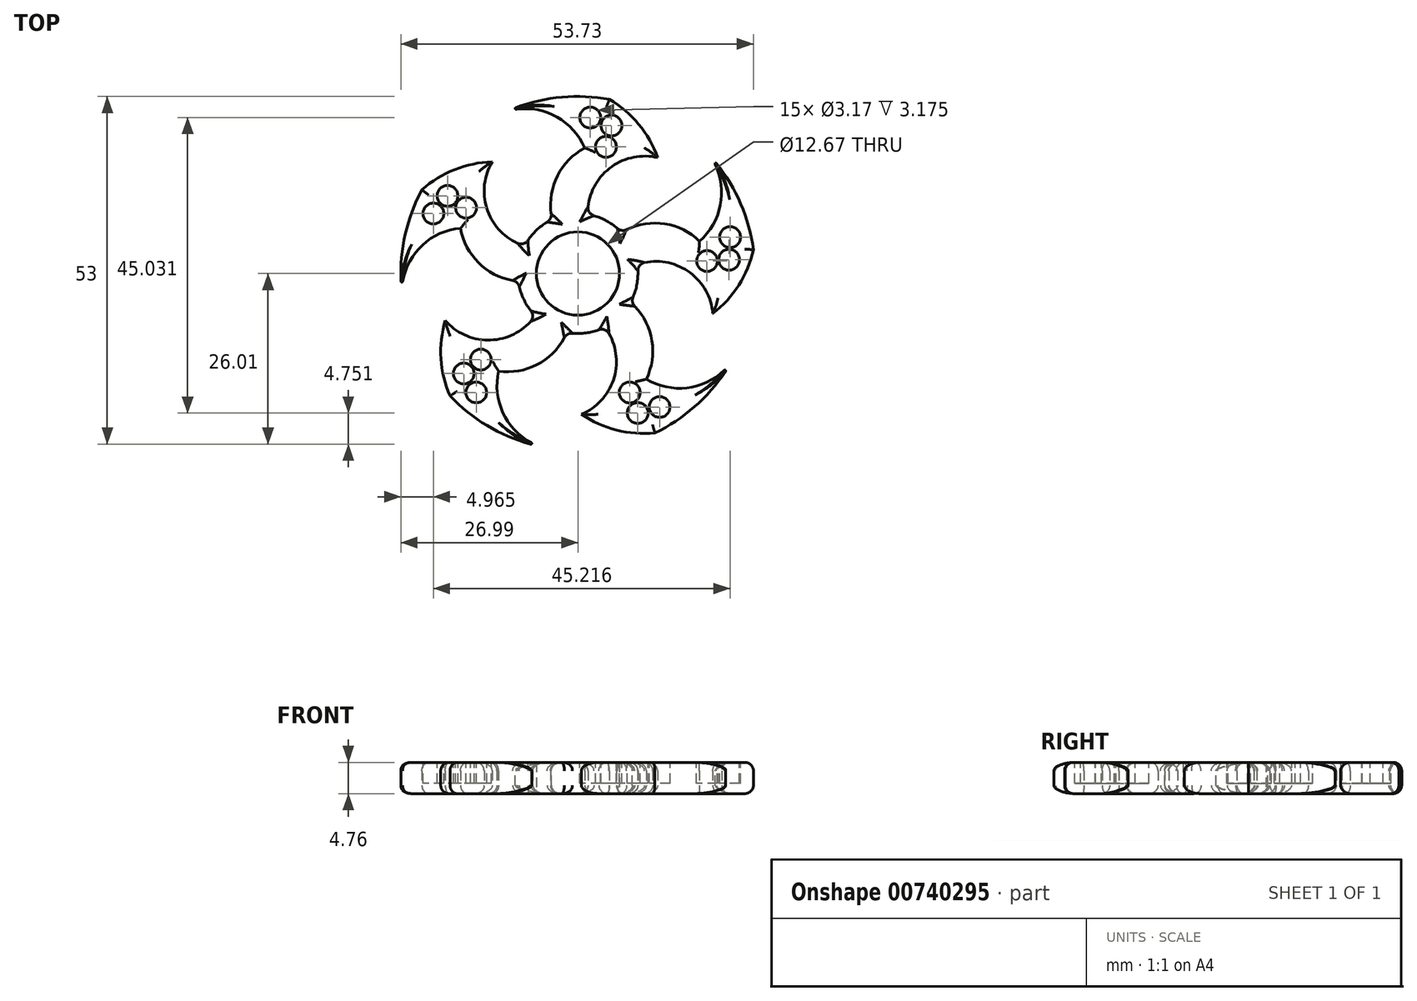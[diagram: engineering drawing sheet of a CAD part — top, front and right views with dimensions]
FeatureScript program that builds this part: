
annotation { "Feature Type Name" : "Feature", "Feature Type Description" : "" }
export const myFeature = defineFeature(function(context is Context, id is Id, definition is map)
    precondition{}
    {
        {
            var Q0;
            Q0=qCreatedBy(makeId("Top.planeOp"),FACE);
            var sketch = newSketch(context, id + "F0", { "sketchPlane" : qUnion([Q0])});
            skCircle(sketch, "E0", {"center": v(0, 0) * mm, "radius": 6.34 * mm});
            skArc(sketch, "E1", {"start": v(-9.07, -1.17) * mm, "mid": v(-8.22, -4) * mm, "end": v(-6.5, -6.43) * mm});
            skArc(sketch, "E2", {"start": v(-23.78, 12.77) * mm, "mid": v(-26.47, 5.28) * mm, "end": v(-26.86, -2.67) * mm});
            skArc(sketch, "E3", {"start": v(-17.89, 6.9) * mm, "mid": v(-24.2, 3.83) * mm, "end": v(-26.86, -2.67) * mm});
            skArc(sketch, "E4", {"start": v(-13.04, 17.02) * mm, "mid": v(-18.79, 15.84) * mm, "end": v(-23.78, 12.77) * mm});
            skArc(sketch, "E5", {"start": v(-17.89, 6.9) * mm, "mid": v(-14.85, 1.36) * mm, "end": v(-9.07, -1.17) * mm});
            skArc(sketch, "E6", {"start": v(-13.04, 17.02) * mm, "mid": v(-13.72, 9.4) * mm, "end": v(-8.12, 4.2) * mm});
            skArc(sketch, "E7.1.0", {"start": v(-20.22, -7.15) * mm, "mid": v(-20.87, -12.97) * mm, "end": v(-19.49, -18.67) * mm});
            skArc(sketch, "E7.1.1", {"start": v(-20.22, -7.15) * mm, "mid": v(-13.19, -10.14) * mm, "end": v(-6.5, -6.43) * mm});
            skArc(sketch, "E7.1.2", {"start": v(-12.09, -14.88) * mm, "mid": v(-5.89, -13.7) * mm, "end": v(-1.7, -8.99) * mm});
            skArc(sketch, "E7.1.3", {"start": v(-12.09, -14.88) * mm, "mid": v(-11.12, -21.83) * mm, "end": v(-5.76, -26.37) * mm});
            skArc(sketch, "E7.2.0", {"start": v(0.55, -21.44) * mm, "mid": v(5.89, -23.86) * mm, "end": v(11.73, -24.3) * mm});
            skArc(sketch, "E7.2.1", {"start": v(0.55, -21.44) * mm, "mid": v(5.57, -15.67) * mm, "end": v(4.1, -8.17) * mm});
            skArc(sketch, "E7.2.2", {"start": v(10.42, -16.1) * mm, "mid": v(11.21, -9.83) * mm, "end": v(8.02, -4.39) * mm});
            skArc(sketch, "E7.2.3", {"start": v(10.42, -16.1) * mm, "mid": v(17.33, -17.32) * mm, "end": v(23.3, -13.63) * mm});
            skArc(sketch, "E7.3.0", {"start": v(20.56, -6.1) * mm, "mid": v(24.5, -1.77) * mm, "end": v(26.74, 3.65) * mm});
            skArc(sketch, "E7.3.1", {"start": v(20.56, -6.1) * mm, "mid": v(16.63, 0.45) * mm, "end": v(9.04, 1.38) * mm});
            skArc(sketch, "E7.3.2", {"start": v(18.52, 4.93) * mm, "mid": v(12.82, 7.63) * mm, "end": v(6.65, 6.27) * mm});
            skArc(sketch, "E7.3.3", {"start": v(18.52, 4.93) * mm, "mid": v(21.83, 11.13) * mm, "end": v(20.16, 17.94) * mm});
            skArc(sketch, "E7.4.0", {"start": v(12.16, 17.67) * mm, "mid": v(9.26, 22.76) * mm, "end": v(4.8, 26.56) * mm});
            skArc(sketch, "E7.4.1", {"start": v(12.16, 17.67) * mm, "mid": v(4.71, 15.95) * mm, "end": v(1.49, 9.02) * mm});
            skArc(sketch, "E7.4.2", {"start": v(1.03, 19.14) * mm, "mid": v(-3.3, 14.55) * mm, "end": v(-3.91, 8.26) * mm});
            skArc(sketch, "E7.4.3", {"start": v(1.03, 19.14) * mm, "mid": v(-3.84, 24.2) * mm, "end": v(-10.84, 24.72) * mm});
            skArc(sketch, "E8.trimOffspring", {"start": v(4.8, 26.56) * mm, "mid": v(-3.16, 26.8) * mm, "end": v(-10.84, 24.72) * mm});
            skArc(sketch, "E9.trimOffspring", {"start": v(26.74, 3.65) * mm, "mid": v(24.51, 11.29) * mm, "end": v(20.16, 17.94) * mm});
            skArc(sketch, "E10.trimOffspring", {"start": v(11.73, -24.3) * mm, "mid": v(18.3, -19.83) * mm, "end": v(23.3, -13.63) * mm});
            skArc(sketch, "E11.trimOffspring", {"start": v(-19.49, -18.67) * mm, "mid": v(-13.2, -23.54) * mm, "end": v(-5.76, -26.37) * mm});
            skArc(sketch, "E12.trimOffspring", {"start": v(-1.7, -8.99) * mm, "mid": v(1.27, -9.06) * mm, "end": v(4.1, -8.17) * mm});
            skArc(sketch, "E13.trimOffspring", {"start": v(8.02, -4.39) * mm, "mid": v(9, -1.59) * mm, "end": v(9.04, 1.38) * mm});
            skArc(sketch, "E14.trimOffspring", {"start": v(6.65, 6.27) * mm, "mid": v(4.3, 8.07) * mm, "end": v(1.49, 9.02) * mm});
            skArc(sketch, "E15.trimOffspring", {"start": v(-3.91, 8.26) * mm, "mid": v(-6.35, 6.58) * mm, "end": v(-8.12, 4.2) * mm});
            skSolve(sketch);
        }
        {
            var Q0;
            Q0 = qSketchRegion(id + "F0", true);
            extrude(context, id + "F1", {"entities" : qUnion([Q0]), "depth" : 4.76 * mm, "offsetDistance" : 25.4 * mm});
        }
        {
            var Q0;
            Q0=makeQuery(id+"F1.opExtrude","CAP_EDGE",EDGE,{"disambiguationData":[OSD([sQuery(id+"F0.wireOp",EDGE,"E5")])],"isStart":false});
            var Q1;
            Q1=makeQuery(id+"F1.opExtrude","CAP_EDGE",EDGE,{"disambiguationData":[OSD([sQuery(id+"F0.wireOp",EDGE,"E3")])],"isStart":false});
            var Q2;
            Q2=makeQuery(id+"F1.opExtrude","CAP_EDGE",EDGE,{"disambiguationData":[OSD([sQuery(id+"F0.wireOp",EDGE,"E2")])],"isStart":false});
            var Q3;
            Q3=makeQuery(id+"F1.opExtrude","CAP_EDGE",EDGE,{"disambiguationData":[OSD([sQuery(id+"F0.wireOp",EDGE,"E4")])],"isStart":false});
            var Q4;
            Q4=makeQuery(id+"F1.opExtrude","CAP_EDGE",EDGE,{"disambiguationData":[OSD([sQuery(id+"F0.wireOp",EDGE,"E6")])],"isStart":false});
            var Q5;
            Q5=makeQuery(id+"F1.opExtrude","CAP_EDGE",EDGE,{"disambiguationData":[OSD([sQuery(id+"F0.wireOp",EDGE,"E15.trimOffspring")])],"isStart":false});
            var Q6;
            Q6=makeQuery(id+"F1.opExtrude","CAP_EDGE",EDGE,{"disambiguationData":[OSD([sQuery(id+"F0.wireOp",EDGE,"E7.4.2")])],"isStart":false});
            var Q7;
            Q7=makeQuery(id+"F1.opExtrude","CAP_EDGE",EDGE,{"disambiguationData":[OSD([sQuery(id+"F0.wireOp",EDGE,"E7.4.3")])],"isStart":false});
            var Q8;
            Q8=makeQuery(id+"F1.opExtrude","CAP_EDGE",EDGE,{"disambiguationData":[OSD([sQuery(id+"F0.wireOp",EDGE,"E8.trimOffspring")])],"isStart":false});
            var Q9;
            Q9=makeQuery(id+"F1.opExtrude","CAP_EDGE",EDGE,{"disambiguationData":[OSD([sQuery(id+"F0.wireOp",EDGE,"E7.4.0")])],"isStart":false});
            var Q10;
            Q10=makeQuery(id+"F1.opExtrude","CAP_EDGE",EDGE,{"disambiguationData":[OSD([sQuery(id+"F0.wireOp",EDGE,"E7.4.1")])],"isStart":false});
            var Q11;
            Q11=makeQuery(id+"F1.opExtrude","CAP_EDGE",EDGE,{"disambiguationData":[OSD([sQuery(id+"F0.wireOp",EDGE,"E14.trimOffspring")])],"isStart":false});
            var Q12;
            Q12=makeQuery(id+"F1.opExtrude","CAP_EDGE",EDGE,{"disambiguationData":[OSD([sQuery(id+"F0.wireOp",EDGE,"E7.3.2")])],"isStart":false});
            var Q13;
            Q13=makeQuery(id+"F1.opExtrude","CAP_EDGE",EDGE,{"disambiguationData":[OSD([sQuery(id+"F0.wireOp",EDGE,"E7.3.3")])],"isStart":false});
            var Q14;
            Q14=makeQuery(id+"F1.opExtrude","CAP_EDGE",EDGE,{"disambiguationData":[OSD([sQuery(id+"F0.wireOp",EDGE,"E9.trimOffspring")])],"isStart":false});
            var Q15;
            Q15=makeQuery(id+"F1.opExtrude","CAP_EDGE",EDGE,{"disambiguationData":[OSD([sQuery(id+"F0.wireOp",EDGE,"E7.3.0")])],"isStart":false});
            var Q16;
            Q16=makeQuery(id+"F1.opExtrude","CAP_EDGE",EDGE,{"disambiguationData":[OSD([sQuery(id+"F0.wireOp",EDGE,"E7.3.1")])],"isStart":false});
            var Q17;
            Q17=makeQuery(id+"F1.opExtrude","CAP_EDGE",EDGE,{"disambiguationData":[OSD([sQuery(id+"F0.wireOp",EDGE,"E13.trimOffspring")])],"isStart":false});
            var Q18;
            Q18=makeQuery(id+"F1.opExtrude","CAP_EDGE",EDGE,{"disambiguationData":[OSD([sQuery(id+"F0.wireOp",EDGE,"E7.2.2")])],"isStart":false});
            var Q19;
            Q19=makeQuery(id+"F1.opExtrude","CAP_EDGE",EDGE,{"disambiguationData":[OSD([sQuery(id+"F0.wireOp",EDGE,"E7.2.3")])],"isStart":false});
            var Q20;
            Q20=makeQuery(id+"F1.opExtrude","CAP_EDGE",EDGE,{"disambiguationData":[OSD([sQuery(id+"F0.wireOp",EDGE,"E10.trimOffspring")])],"isStart":false});
            var Q21;
            Q21=makeQuery(id+"F1.opExtrude","CAP_EDGE",EDGE,{"disambiguationData":[OSD([sQuery(id+"F0.wireOp",EDGE,"E7.2.0")])],"isStart":false});
            var Q22;
            Q22=makeQuery(id+"F1.opExtrude","CAP_EDGE",EDGE,{"disambiguationData":[OSD([sQuery(id+"F0.wireOp",EDGE,"E7.2.1")])],"isStart":false});
            var Q23;
            Q23=makeQuery(id+"F1.opExtrude","CAP_EDGE",EDGE,{"disambiguationData":[OSD([sQuery(id+"F0.wireOp",EDGE,"E12.trimOffspring")])],"isStart":false});
            var Q24;
            Q24=makeQuery(id+"F1.opExtrude","CAP_EDGE",EDGE,{"disambiguationData":[OSD([sQuery(id+"F0.wireOp",EDGE,"E7.1.2")])],"isStart":false});
            var Q25;
            Q25=makeQuery(id+"F1.opExtrude","CAP_EDGE",EDGE,{"disambiguationData":[OSD([sQuery(id+"F0.wireOp",EDGE,"E7.1.3")])],"isStart":false});
            var Q26;
            Q26=makeQuery(id+"F1.opExtrude","CAP_EDGE",EDGE,{"disambiguationData":[OSD([sQuery(id+"F0.wireOp",EDGE,"E11.trimOffspring")])],"isStart":false});
            var Q27;
            Q27=makeQuery(id+"F1.opExtrude","CAP_EDGE",EDGE,{"disambiguationData":[OSD([sQuery(id+"F0.wireOp",EDGE,"E7.1.0")])],"isStart":false});
            var Q28;
            Q28=makeQuery(id+"F1.opExtrude","CAP_EDGE",EDGE,{"disambiguationData":[OSD([sQuery(id+"F0.wireOp",EDGE,"E7.1.1")])],"isStart":false});
            var Q29;
            Q29=makeQuery(id+"F1.opExtrude","CAP_EDGE",EDGE,{"disambiguationData":[OSD([sQuery(id+"F0.wireOp",EDGE,"E1")])],"isStart":false});
            var Q30;
            Q30=makeQuery(id+"F1.opExtrude","CAP_EDGE",EDGE,{"disambiguationData":[OSD([sQuery(id+"F0.wireOp",EDGE,"E7.1.0")])],"isStart":true});
            var Q31;
            Q31=makeQuery(id+"F1.opExtrude","CAP_EDGE",EDGE,{"disambiguationData":[OSD([sQuery(id+"F0.wireOp",EDGE,"E11.trimOffspring")])],"isStart":true});
            var Q32;
            Q32=makeQuery(id+"F1.opExtrude","CAP_EDGE",EDGE,{"disambiguationData":[OSD([sQuery(id+"F0.wireOp",EDGE,"E7.1.3")])],"isStart":true});
            var Q33;
            Q33=makeQuery(id+"F1.opExtrude","CAP_EDGE",EDGE,{"disambiguationData":[OSD([sQuery(id+"F0.wireOp",EDGE,"E7.1.2")])],"isStart":true});
            var Q34;
            Q34=makeQuery(id+"F1.opExtrude","CAP_EDGE",EDGE,{"disambiguationData":[OSD([sQuery(id+"F0.wireOp",EDGE,"E12.trimOffspring")])],"isStart":true});
            var Q35;
            Q35=makeQuery(id+"F1.opExtrude","CAP_EDGE",EDGE,{"disambiguationData":[OSD([sQuery(id+"F0.wireOp",EDGE,"E7.2.1")])],"isStart":true});
            var Q36;
            Q36=makeQuery(id+"F1.opExtrude","CAP_EDGE",EDGE,{"disambiguationData":[OSD([sQuery(id+"F0.wireOp",EDGE,"E7.2.0")])],"isStart":true});
            var Q37;
            Q37=makeQuery(id+"F1.opExtrude","CAP_EDGE",EDGE,{"disambiguationData":[OSD([sQuery(id+"F0.wireOp",EDGE,"E10.trimOffspring")])],"isStart":true});
            var Q38;
            Q38=makeQuery(id+"F1.opExtrude","CAP_EDGE",EDGE,{"disambiguationData":[OSD([sQuery(id+"F0.wireOp",EDGE,"E7.2.3")])],"isStart":true});
            var Q39;
            Q39=makeQuery(id+"F1.opExtrude","CAP_EDGE",EDGE,{"disambiguationData":[OSD([sQuery(id+"F0.wireOp",EDGE,"E7.2.2")])],"isStart":true});
            var Q40;
            Q40=makeQuery(id+"F1.opExtrude","CAP_EDGE",EDGE,{"disambiguationData":[OSD([sQuery(id+"F0.wireOp",EDGE,"E13.trimOffspring")])],"isStart":true});
            var Q41;
            Q41=makeQuery(id+"F1.opExtrude","CAP_EDGE",EDGE,{"disambiguationData":[OSD([sQuery(id+"F0.wireOp",EDGE,"E7.3.1")])],"isStart":true});
            var Q42;
            Q42=makeQuery(id+"F1.opExtrude","CAP_EDGE",EDGE,{"disambiguationData":[OSD([sQuery(id+"F0.wireOp",EDGE,"E7.3.0")])],"isStart":true});
            var Q43;
            Q43=makeQuery(id+"F1.opExtrude","CAP_EDGE",EDGE,{"disambiguationData":[OSD([sQuery(id+"F0.wireOp",EDGE,"E9.trimOffspring")])],"isStart":true});
            var Q44;
            Q44=makeQuery(id+"F1.opExtrude","CAP_EDGE",EDGE,{"disambiguationData":[OSD([sQuery(id+"F0.wireOp",EDGE,"E7.3.3")])],"isStart":true});
            var Q45;
            Q45=makeQuery(id+"F1.opExtrude","CAP_EDGE",EDGE,{"disambiguationData":[OSD([sQuery(id+"F0.wireOp",EDGE,"E7.3.2")])],"isStart":true});
            var Q46;
            Q46=makeQuery(id+"F1.opExtrude","CAP_EDGE",EDGE,{"disambiguationData":[OSD([sQuery(id+"F0.wireOp",EDGE,"E14.trimOffspring")])],"isStart":true});
            var Q47;
            Q47=makeQuery(id+"F1.opExtrude","CAP_EDGE",EDGE,{"disambiguationData":[OSD([sQuery(id+"F0.wireOp",EDGE,"E7.4.1")])],"isStart":true});
            var Q48;
            Q48=makeQuery(id+"F1.opExtrude","CAP_EDGE",EDGE,{"disambiguationData":[OSD([sQuery(id+"F0.wireOp",EDGE,"E7.4.0")])],"isStart":true});
            var Q49;
            Q49=makeQuery(id+"F1.opExtrude","CAP_EDGE",EDGE,{"disambiguationData":[OSD([sQuery(id+"F0.wireOp",EDGE,"E7.1.1")])],"isStart":true});
            var Q50;
            Q50=makeQuery(id+"F1.opExtrude","CAP_EDGE",EDGE,{"disambiguationData":[OSD([sQuery(id+"F0.wireOp",EDGE,"E1")])],"isStart":true});
            var Q51;
            Q51=makeQuery(id+"F1.opExtrude","CAP_EDGE",EDGE,{"disambiguationData":[OSD([sQuery(id+"F0.wireOp",EDGE,"E5")])],"isStart":true});
            var Q52;
            Q52=makeQuery(id+"F1.opExtrude","CAP_EDGE",EDGE,{"disambiguationData":[OSD([sQuery(id+"F0.wireOp",EDGE,"E3")])],"isStart":true});
            var Q53;
            Q53=makeQuery(id+"F1.opExtrude","CAP_EDGE",EDGE,{"disambiguationData":[OSD([sQuery(id+"F0.wireOp",EDGE,"E2")])],"isStart":true});
            var Q54;
            Q54=makeQuery(id+"F1.opExtrude","CAP_EDGE",EDGE,{"disambiguationData":[OSD([sQuery(id+"F0.wireOp",EDGE,"E4")])],"isStart":true});
            var Q55;
            Q55=makeQuery(id+"F1.opExtrude","CAP_EDGE",EDGE,{"disambiguationData":[OSD([sQuery(id+"F0.wireOp",EDGE,"E6")])],"isStart":true});
            var Q56;
            Q56=makeQuery(id+"F1.opExtrude","CAP_EDGE",EDGE,{"disambiguationData":[OSD([sQuery(id+"F0.wireOp",EDGE,"E15.trimOffspring")])],"isStart":true});
            var Q57;
            Q57=makeQuery(id+"F1.opExtrude","CAP_EDGE",EDGE,{"disambiguationData":[OSD([sQuery(id+"F0.wireOp",EDGE,"E7.4.2")])],"isStart":true});
            var Q58;
            Q58=makeQuery(id+"F1.opExtrude","CAP_EDGE",EDGE,{"disambiguationData":[OSD([sQuery(id+"F0.wireOp",EDGE,"E7.4.3")])],"isStart":true});
            var Q59;
            Q59=makeQuery(id+"F1.opExtrude","CAP_EDGE",EDGE,{"disambiguationData":[OSD([sQuery(id+"F0.wireOp",EDGE,"E8.trimOffspring")])],"isStart":true});
            fillet(context, id + "F2", {"entities" : qUnion([Q0, Q1, Q2, Q3, Q4, Q5, Q6, Q7, Q8, Q9, Q10, Q11, Q12, Q13, Q14, Q15, Q16, Q17, Q18, Q19, Q20, Q21, Q22, Q23, Q24, Q25, Q26, Q27, Q28, Q29, Q30, Q31, Q32, Q33, Q34, Q35, Q36, Q37, Q38, Q39, Q40, Q41, Q42, Q43, Q44, Q45, Q46, Q47, Q48, Q49, Q50, Q51, Q52, Q53, Q54, Q55, Q56, Q57, Q58, Q59]), "radius" : 1.27 * mm, "tangentPropagation" : true, "allowEdgeOverflow" : false});
        }
        {
            var Q0;
            Q0=makeQuery(id+"F1.opExtrude","SWEPT_EDGE",EDGE,{"disambiguationData":[OSD([sQuery(id+"F0.wireOp",EDGE,"E6"),sQuery(id+"F0.wireOp",EDGE,"E15.trimOffspring")])]});
            var Q1;
            Q1=makeQuery(id+"F1.opExtrude","SWEPT_EDGE",EDGE,{"disambiguationData":[OSD([sQuery(id+"F0.wireOp",EDGE,"E7.4.2"),sQuery(id+"F0.wireOp",EDGE,"E15.trimOffspring")])]});
            var Q2;
            Q2=makeQuery(id+"F1.opExtrude","SWEPT_EDGE",EDGE,{"disambiguationData":[OSD([sQuery(id+"F0.wireOp",EDGE,"E1"),sQuery(id+"F0.wireOp",EDGE,"E7.1.1")])]});
            var Q3;
            Q3=makeQuery(id+"F1.opExtrude","SWEPT_EDGE",EDGE,{"disambiguationData":[OSD([sQuery(id+"F0.wireOp",EDGE,"E1"),sQuery(id+"F0.wireOp",EDGE,"E5")])]});
            var Q4;
            Q4=makeQuery(id+"F1.opExtrude","SWEPT_EDGE",EDGE,{"disambiguationData":[OSD([sQuery(id+"F0.wireOp",EDGE,"E7.4.1"),sQuery(id+"F0.wireOp",EDGE,"E14.trimOffspring")])]});
            var Q5;
            Q5=makeQuery(id+"F1.opExtrude","SWEPT_EDGE",EDGE,{"disambiguationData":[OSD([sQuery(id+"F0.wireOp",EDGE,"E7.2.2"),sQuery(id+"F0.wireOp",EDGE,"E13.trimOffspring")])]});
            var Q6;
            Q6=makeQuery(id+"F1.opExtrude","SWEPT_EDGE",EDGE,{"disambiguationData":[OSD([sQuery(id+"F0.wireOp",EDGE,"E7.3.1"),sQuery(id+"F0.wireOp",EDGE,"E13.trimOffspring")])]});
            var Q7;
            Q7=makeQuery(id+"F1.opExtrude","SWEPT_EDGE",EDGE,{"disambiguationData":[OSD([sQuery(id+"F0.wireOp",EDGE,"E7.3.2"),sQuery(id+"F0.wireOp",EDGE,"E14.trimOffspring")])]});
            var Q8;
            Q8=makeQuery(id+"F1.opExtrude","SWEPT_EDGE",EDGE,{"disambiguationData":[OSD([sQuery(id+"F0.wireOp",EDGE,"E7.1.2"),sQuery(id+"F0.wireOp",EDGE,"E12.trimOffspring")])]});
            var Q9;
            Q9=makeQuery(id+"F1.opExtrude","SWEPT_EDGE",EDGE,{"disambiguationData":[OSD([sQuery(id+"F0.wireOp",EDGE,"E7.2.1"),sQuery(id+"F0.wireOp",EDGE,"E12.trimOffspring")])]});
            fillet(context, id + "F3", {"entities" : qUnion([Q0, Q1, Q2, Q3, Q4, Q5, Q6, Q7, Q8, Q9]), "radius" : 1.27 * mm, "tangentPropagation" : true, "allowEdgeOverflow" : false});
        }
        {
            var Q0;
            Q0=makeQuery(id+"F1.opExtrude","SWEPT_EDGE",EDGE,{"disambiguationData":[OSD([sQuery(id+"F0.wireOp",EDGE,"E7.4.3"),sQuery(id+"F0.wireOp",EDGE,"E8.trimOffspring")])]});
            var Q1;
            Q1=makeQuery(id+"F1.opExtrude","SWEPT_EDGE",EDGE,{"disambiguationData":[OSD([sQuery(id+"F0.wireOp",EDGE,"E2"),sQuery(id+"F0.wireOp",EDGE,"E3")])]});
            var Q2;
            Q2=makeQuery(id+"F1.opExtrude","SWEPT_EDGE",EDGE,{"disambiguationData":[OSD([sQuery(id+"F0.wireOp",EDGE,"E7.1.3"),sQuery(id+"F0.wireOp",EDGE,"E11.trimOffspring")])]});
            var Q3;
            Q3=makeQuery(id+"F1.opExtrude","SWEPT_EDGE",EDGE,{"disambiguationData":[OSD([sQuery(id+"F0.wireOp",EDGE,"E7.2.3"),sQuery(id+"F0.wireOp",EDGE,"E10.trimOffspring")])]});
            var Q4;
            Q4=makeQuery(id+"F1.opExtrude","SWEPT_EDGE",EDGE,{"disambiguationData":[OSD([sQuery(id+"F0.wireOp",EDGE,"E7.3.3"),sQuery(id+"F0.wireOp",EDGE,"E9.trimOffspring")])]});
            fillet(context, id + "F4", {"entities" : qUnion([Q0, Q1, Q2, Q3, Q4]), "radius" : 0.13 * mm, "tangentPropagation" : true, "allowEdgeOverflow" : false});
        }
        {
            var Q0;
            Q0=makeQuery(id+"F1.opExtrude","CAP_FACE",FACE,{"disambiguationData":[OSD([sQuery(id+"F0.wireOp",EDGE,"E0"),sQuery(id+"F0.wireOp",EDGE,"E1"),sQuery(id+"F0.wireOp",EDGE,"E2"),sQuery(id+"F0.wireOp",EDGE,"E3"),sQuery(id+"F0.wireOp",EDGE,"E4"),sQuery(id+"F0.wireOp",EDGE,"E5"),sQuery(id+"F0.wireOp",EDGE,"E6"),sQuery(id+"F0.wireOp",EDGE,"E7.1.0"),sQuery(id+"F0.wireOp",EDGE,"E7.1.1"),sQuery(id+"F0.wireOp",EDGE,"E7.1.2"),sQuery(id+"F0.wireOp",EDGE,"E7.1.3"),sQuery(id+"F0.wireOp",EDGE,"E7.2.0"),sQuery(id+"F0.wireOp",EDGE,"E7.2.1"),sQuery(id+"F0.wireOp",EDGE,"E7.2.2"),sQuery(id+"F0.wireOp",EDGE,"E7.2.3"),sQuery(id+"F0.wireOp",EDGE,"E7.3.0"),sQuery(id+"F0.wireOp",EDGE,"E7.3.1"),sQuery(id+"F0.wireOp",EDGE,"E7.3.2"),sQuery(id+"F0.wireOp",EDGE,"E7.3.3"),sQuery(id+"F0.wireOp",EDGE,"E7.4.0"),sQuery(id+"F0.wireOp",EDGE,"E7.4.1"),sQuery(id+"F0.wireOp",EDGE,"E7.4.2"),sQuery(id+"F0.wireOp",EDGE,"E7.4.3"),sQuery(id+"F0.wireOp",EDGE,"E8.trimOffspring"),sQuery(id+"F0.wireOp",EDGE,"E9.trimOffspring"),sQuery(id+"F0.wireOp",EDGE,"E10.trimOffspring"),sQuery(id+"F0.wireOp",EDGE,"E11.trimOffspring"),sQuery(id+"F0.wireOp",EDGE,"E12.trimOffspring"),sQuery(id+"F0.wireOp",EDGE,"E13.trimOffspring"),sQuery(id+"F0.wireOp",EDGE,"E14.trimOffspring"),sQuery(id+"F0.wireOp",EDGE,"E15.trimOffspring")])],"isStart":false});
            var sketch = newSketch(context, id + "F5", { "sketchPlane" : qUnion([Q0])});
            skCircle(sketch, "E16", {"center": v(1.89, 23.77) * mm, "radius": 1.59 * mm});
            skCircle(sketch, "E17", {"center": v(5.12, 22.56) * mm, "radius": 1.59 * mm});
            skCircle(sketch, "E18", {"center": v(4.27, 19.3) * mm, "radius": 1.59 * mm});
            skCircle(sketch, "E19.1.0", {"center": v(-22.03, 9.14) * mm, "radius": 1.59 * mm});
            skCircle(sketch, "E19.1.1", {"center": v(-19.87, 11.84) * mm, "radius": 1.59 * mm});
            skCircle(sketch, "E19.1.2", {"center": v(-17.04, 10.03) * mm, "radius": 1.59 * mm});
            skCircle(sketch, "E19.2.0", {"center": v(-15.5, -18.12) * mm, "radius": 1.59 * mm});
            skCircle(sketch, "E19.2.1", {"center": v(-17.4, -15.24) * mm, "radius": 1.59 * mm});
            skCircle(sketch, "E19.2.2", {"center": v(-14.8, -13.1) * mm, "radius": 1.59 * mm});
            skCircle(sketch, "E19.3.0", {"center": v(12.45, -20.34) * mm, "radius": 1.59 * mm});
            skCircle(sketch, "E19.3.1", {"center": v(9.12, -21.26) * mm, "radius": 1.59 * mm});
            skCircle(sketch, "E19.3.2", {"center": v(7.9, -18.13) * mm, "radius": 1.59 * mm});
            skCircle(sketch, "E19.4.0", {"center": v(23.2, 5.55) * mm, "radius": 1.59 * mm});
            skCircle(sketch, "E19.4.1", {"center": v(23.04, 2.1) * mm, "radius": 1.59 * mm});
            skCircle(sketch, "E19.4.2", {"center": v(19.68, 1.9) * mm, "radius": 1.59 * mm});
            skPoint(sketch, "E19.center", {"position": v(0, 0) * mm});
            skSolve(sketch);
        }
        {
            var Q0;
            Q0 = qSketchRegion(id + "F5", true);
            extrude(context, id + "F6", {"entities" : qUnion([Q0]), "operationType" : NewBodyOperationType.REMOVE, "oppositeDirection" : true, "depth" : 3.17 * mm, "offsetDistance" : 25.4 * mm});
        }
    });
